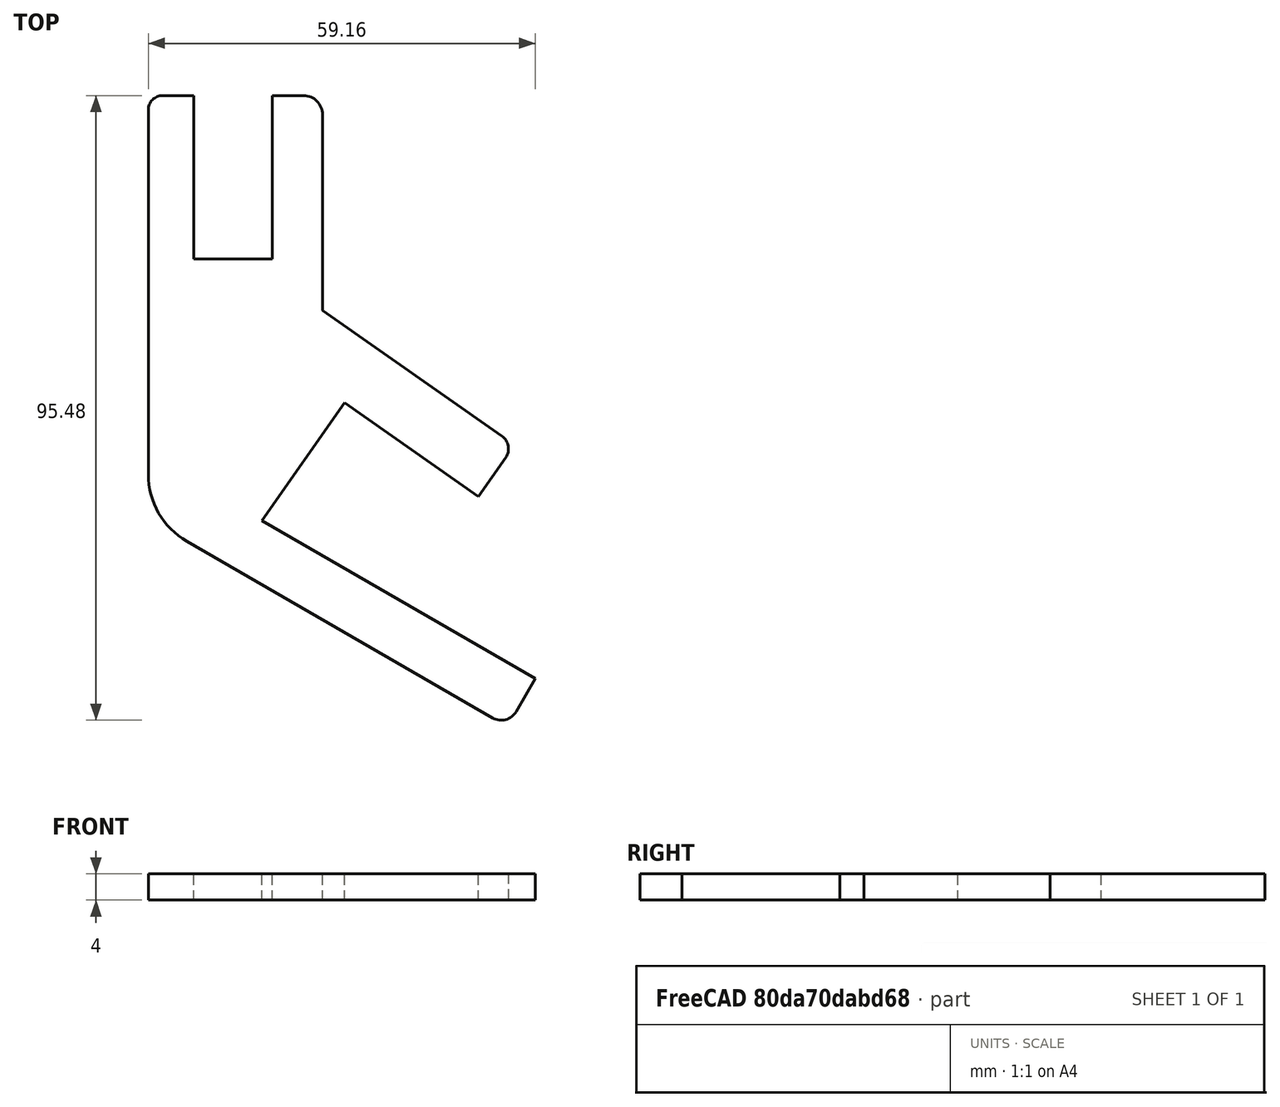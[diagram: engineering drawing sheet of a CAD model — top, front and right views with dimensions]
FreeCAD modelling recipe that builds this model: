
FCSTD DOCUMENT  (FreeCAD 0.14R3702 (Git))
Label: dock_teclado_movil
License: CC-BY 3.0
LicenseURL: http://creativecommons.org/licenses/by/3.0/
objects: Sketcher::SketchObject×1, PartDesign::Pad×1
note: 3 computed .brp shape members not serialized (recipe doc carries the construction recipe); baked Part::Feature solids carry a one-line shape summary decoded from their .brp

FEATURE [Sketcher::SketchObject] Sketch
  sketch-geometry (19):
    g0: LineSegment StartX=-10.7581 StartY=41.6036 StartZ=0 EndX=-6 EndY=41.6036 EndZ=0
    g1: LineSegment StartX=-6 StartY=41.6036 StartZ=0 EndX=-6 EndY=16.6036 EndZ=0
    g2: LineSegment StartX=-6 StartY=16.6036 StartZ=0 EndX=6 EndY=16.6036 EndZ=0
    g3: LineSegment StartX=6 StartY=16.6036 StartZ=0 EndX=6 EndY=41.6036 EndZ=0
    g4: LineSegment StartX=6 StartY=41.6036 StartZ=0 EndX=10.7581 EndY=41.6036 EndZ=0
    g5: LineSegment StartX=13.6756 StartY=38.686 StartZ=0 EndX=13.6756 EndY=8.75346 EndZ=0
    g6: LineSegment StartX=13.6756 StartY=8.75346 StartZ=0 EndX=41.0723 EndY=-10.4299 EndZ=0
    g7: LineSegment StartX=41.6595 StartY=-13.7603 StartZ=0 EndX=37.5199 EndY=-19.6723 EndZ=0
    g8: LineSegment StartX=37.5199 StartY=-19.6723 StartZ=0 EndX=17.0411 EndY=-5.33292 EndZ=0
    g9: LineSegment StartX=17.0411 StartY=-5.33292 StartZ=0 EndX=4.42241 EndY=-23.3543 EndZ=0
    g10: LineSegment StartX=4.42241 StartY=-23.3543 StartZ=0 EndX=46.2135 EndY=-47.4824 EndZ=0
    g11: LineSegment StartX=46.2135 StartY=-47.4824 StartZ=0 EndX=43.2789 EndY=-52.5652 EndZ=0
    g12: LineSegment StartX=39.6815 StartY=-53.5292 StartZ=0 EndX=-7.04713 EndY=-26.5504 EndZ=0
    g13: LineSegment StartX=-12.9521 StartY=-16.3227 StartZ=0 EndX=-12.9521 EndY=39.4096 EndZ=0
    g14: ArcOfCircle CenterX=-1.14218 CenterY=-16.3227 CenterZ=0 NormalX=0 NormalY=0 NormalZ=1 Radius=11.8099 StartAngle=3.14159 EndAngle=4.18879
    g15: ArcOfCircle CenterX=-10.7581 CenterY=39.4096 CenterZ=0 NormalX=0 NormalY=0 NormalZ=1 Radius=2.19403 StartAngle=1.5708 EndAngle=3.14159
    g16: ArcOfCircle CenterX=10.7581 CenterY=38.686 CenterZ=0 NormalX=0 NormalY=0 NormalZ=1 Radius=2.91759 StartAngle=0 EndAngle=1.5708
    g17: ArcOfCircle CenterX=39.7007 CenterY=-12.3887 CenterZ=0 NormalX=0 NormalY=0 NormalZ=1 Radius=2.39129 StartAngle=5.67232 EndAngle=7.24312
    g18: ArcOfCircle CenterX=40.9982 CenterY=-51.2485 CenterZ=0 NormalX=0 NormalY=0 NormalZ=1 Radius=2.63345 StartAngle=4.18879 EndAngle=5.75959
  constraints (40):
    c: Horizontal(g0)
    c: Coincident(g0,g1)
    c: Vertical(g1)
    c: Coincident(g1,g2)
    c: Horizontal(g2)
    c: Coincident(g2,g3)
    c: Vertical(g3)
    c: Coincident(g3,g4)
    c: Horizontal(g4)
    c: Vertical(g5)
    c: Coincident(g5,g6)
    c: Coincident(g7,g8)
    c: Coincident(g8,g9)
    c: Coincident(g9,g10)
    c: Coincident(g10,g11)
    c: Vertical(g13)
    c: Equal(g0,g4)
    c: Symmetric(g1,g2,g-2)
    c: Perpendicular(g6,g7)
    c: Parallel(g6,g8)
    c: Distance(g9) = 22
    c: Distance(g2) = 12
    c: Distance(g3) = 25
    c: Equal(g1,g3)
    c: Parallel(g10,g12)
    c: Perpendicular(g12,g11)
    c: Perpendicular(g8,g9)
    c: Angle(g10,g9) = 1.48353
    c: Distance(g8) = 25
    c: Angle(g6,g5) = 2.18166
    c: Tangent(g13,g14)
    c: Tangent(g12,g14)
    c: Tangent(g13,g15)
    c: Tangent(g0,g15)
    c: Tangent(g4,g16)
    c: Tangent(g5,g16)
    c: Tangent(g6,g17)
    c: Tangent(g7,g17)
    c: Tangent(g12,g18)
    c: Tangent(g11,g18)
FEATURE [PartDesign::Pad] Pad
  Length = 4
  Length2 = 100
  Sketch = -> Sketch
  Type = 0
